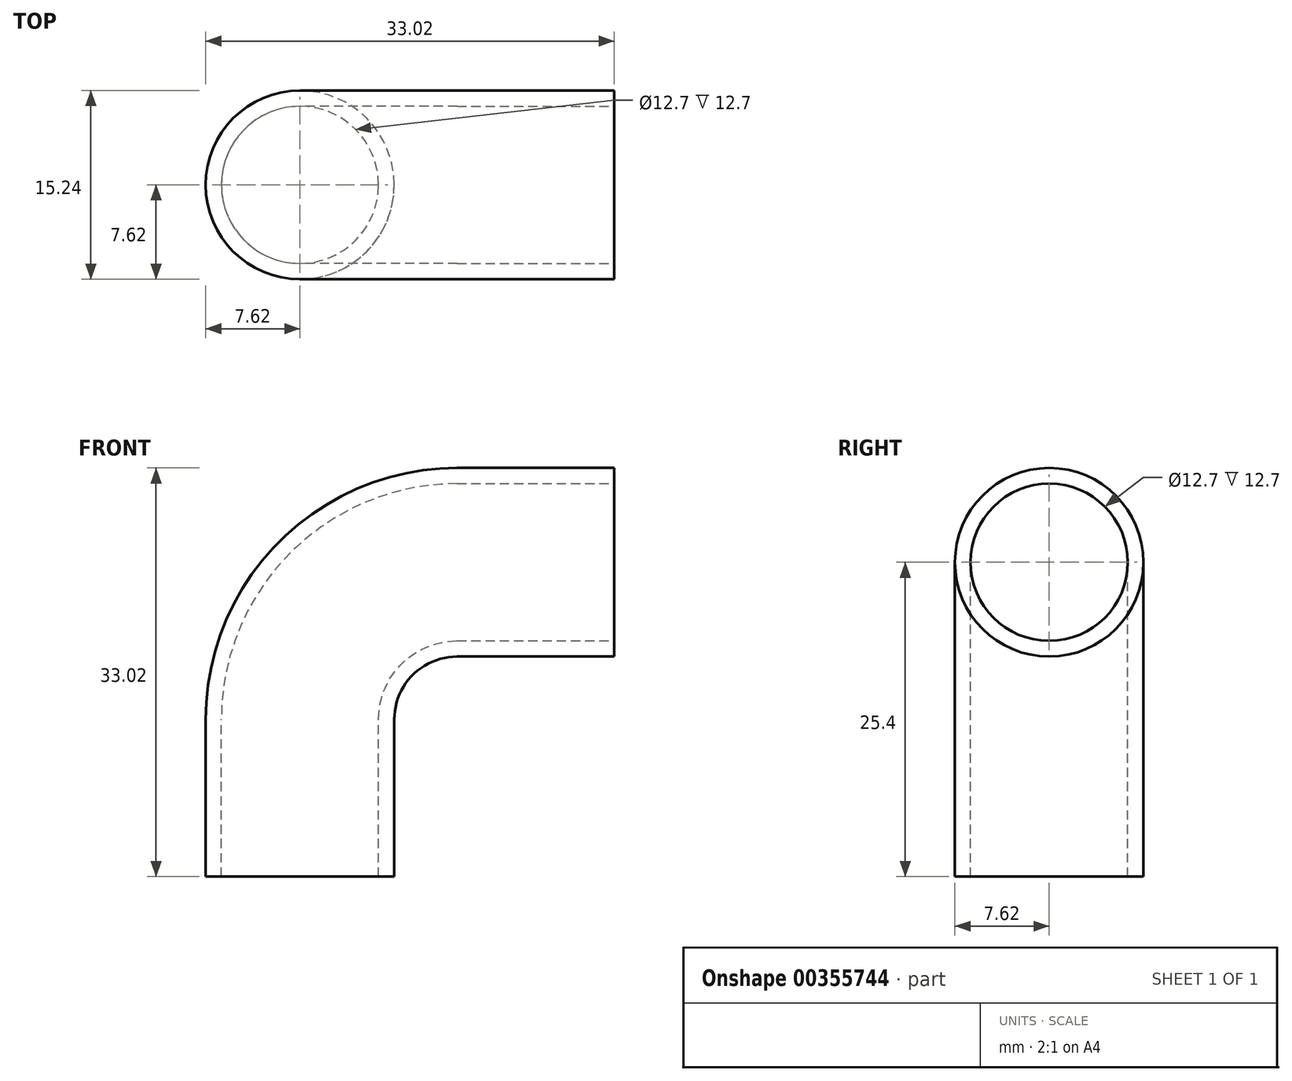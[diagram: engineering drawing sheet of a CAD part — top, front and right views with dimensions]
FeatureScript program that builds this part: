
annotation { "Feature Type Name" : "Feature", "Feature Type Description" : "" }
export const myFeature = defineFeature(function(context is Context, id is Id, definition is map)
    precondition{}
    {
        {
            var Q0;
            Q0=qCreatedBy(makeId("Top.planeOp"),FACE);
            var sketch = newSketch(context, id + "F0", { "sketchPlane" : qUnion([Q0])});
            skCircle(sketch, "E0", {"center": v(0, 0) * mm, "radius": 6.35 * mm});
            skCircle(sketch, "E1", {"center": v(0, 0) * mm, "radius": 7.62 * mm});
            skSolve(sketch);
        }
        {
            var Q0;
            Q0=qCreatedBy(makeId("Front.planeOp"),FACE);
            var sketch = newSketch(context, id + "F1", { "sketchPlane" : qUnion([Q0])});
            skLineSegment(sketch, "E2", {"start": v(0, 0) * mm, "end": v(0, 12.7) * mm});
            skLineSegment(sketch, "E3", {"start": v(12.7, 25.4) * mm, "end": v(25.4, 25.4) * mm});
            skPoint(sketch, "E4.visualSharp", {"position": v(0, 25.4) * mm});
            skArc(sketch, "E4.filletArc", {"start": v(12.7, 25.4) * mm, "mid": v(3.72, 21.68) * mm, "end": v(0, 12.7) * mm});
            skSolve(sketch);
        }
        {
            var Q0;
            Q0 = qSketchRegion(id + "F0", true);
            var Q1;
            Q1 = qConstructionFilter(qBodyType(qCreatedBy(id + "F1" ,EDGE), BodyType.WIRE), ConstructionObject.NO);
            sweep(context, id + "F2", {"profiles" : qUnion([Q0]), "path" : qUnion([Q1])});
        }
    });
